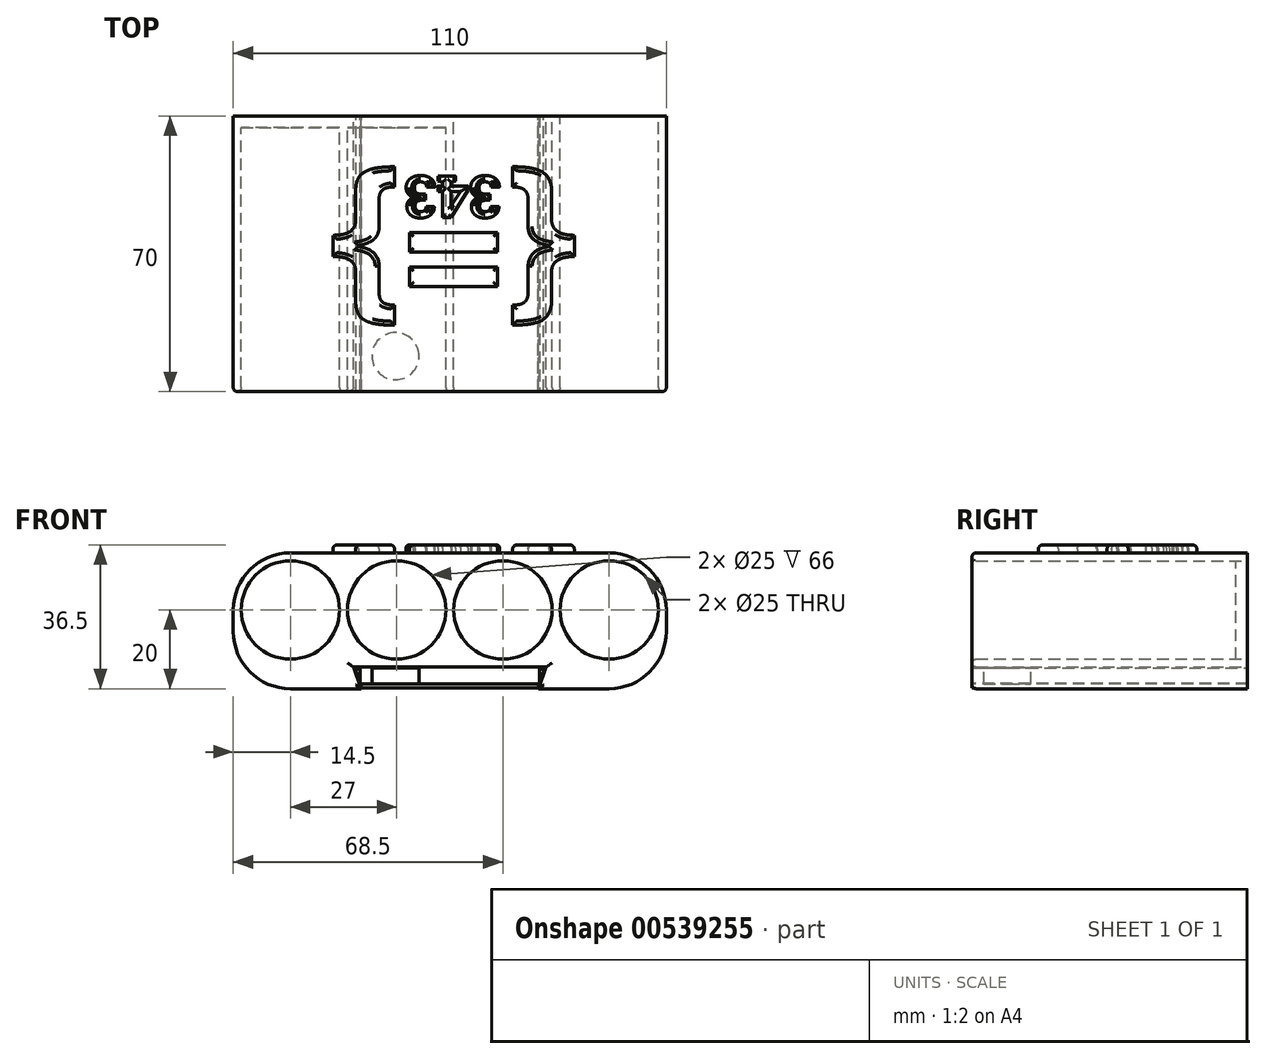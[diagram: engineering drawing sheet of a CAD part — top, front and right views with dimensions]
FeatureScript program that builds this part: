
annotation { "Feature Type Name" : "Feature", "Feature Type Description" : "" }
export const myFeature = defineFeature(function(context is Context, id is Id, definition is map)
    precondition{}
    {
        {
            var Q0;
            Q0=qCreatedBy(makeId("Front.planeOp"),FACE);
            var sketch = newSketch(context, id + "F0", { "sketchPlane" : qUnion([Q0])});
            skLineSegment(sketch, "E0", {"start": v(-24.5, 5.5) * mm, "end": v(-22.5, 0) * mm});
            skLineSegment(sketch, "E1", {"start": v(-22.5, 0) * mm, "end": v(-40.5, 0) * mm});
            skLineSegment(sketch, "E2", {"start": v(-55, 14.5) * mm, "end": v(-55, 20) * mm});
            skPoint(sketch, "E3.visualSharp", {"position": v(-55, 34.5) * mm});
            skArc(sketch, "E3.filletArc", {"start": v(-40.5, 34.5) * mm, "mid": v(-50.75, 30.25) * mm, "end": v(-55, 20) * mm});
            skPoint(sketch, "E4.visualSharp", {"position": v(-55, 0) * mm});
            skArc(sketch, "E4.filletArc", {"start": v(-55, 14.5) * mm, "mid": v(-50.75, 4.25) * mm, "end": v(-40.5, 0) * mm});
            skCircle(sketch, "E5", {"center": v(-40.5, 20) * mm, "radius": 12.5 * mm});
            skCircle(sketch, "E6.1.0.0", {"center": v(-13.5, 20) * mm, "radius": 12.5 * mm});
            skLineSegment(sketch, "E6.direction1", {"start": v(-40.5, 20) * mm, "end": v(-13.5, 20) * mm, "construction": true});
            skLineSegment(sketch, "E7", {"start": v(-40.5, 34.5) * mm, "end": v(-40.5, 0) * mm, "construction": true});
            skLineSegment(sketch, "E8", {"start": v(-40.5, 34.5) * mm, "end": v(0, 34.5) * mm});
            skLineSegment(sketch, "E9", {"start": v(-24.5, 5.5) * mm, "end": v(0, 5.5) * mm});
            skCircle(sketch, "E10.MirrorC", {"center": v(40.5, 20) * mm, "radius": 12.5 * mm});
            skPoint(sketch, "E11.MirrorP", {"position": v(55, 34.5) * mm});
            skLineSegment(sketch, "E12.MirrorCS", {"start": v(22.5, 0) * mm, "end": v(40.5, 0) * mm});
            skArc(sketch, "E13.MirrorCS", {"start": v(55, 14.5) * mm, "mid": v(50.75, 4.25) * mm, "end": v(40.5, 0) * mm});
            skPoint(sketch, "E14.MirrorP", {"position": v(55, 0) * mm});
            skLineSegment(sketch, "E15.MirrorCS", {"start": v(24.5, 5.5) * mm, "end": v(0, 5.5) * mm});
            skArc(sketch, "E16.MirrorCS", {"start": v(40.5, 34.5) * mm, "mid": v(50.75, 30.25) * mm, "end": v(55, 20) * mm});
            skLineSegment(sketch, "E17.MirrorCS", {"start": v(55, 14.5) * mm, "end": v(55, 20) * mm});
            skLineSegment(sketch, "E18.MirrorCS", {"start": v(40.5, 34.5) * mm, "end": v(40.5, 0) * mm, "construction": true});
            skLineSegment(sketch, "E19.MirrorCS", {"start": v(40.5, 34.5) * mm, "end": v(0, 34.5) * mm});
            skLineSegment(sketch, "E20.MirrorCS", {"start": v(24.5, 5.5) * mm, "end": v(22.5, 0) * mm});
            skCircle(sketch, "E21.MirrorC", {"center": v(13.5, 20) * mm, "radius": 12.5 * mm});
            skLineSegment(sketch, "E22.MirrorCS", {"start": v(40.5, 20) * mm, "end": v(13.5, 20) * mm, "construction": true});
            skSolve(sketch);
        }
        {
            var Q0;
            Q0=qSketchRegion(id+"F0",true);
            extrude(context, id + "F1", {"entities" : qUnion([Q0]), "depth" : 70 * mm, "offsetDistance" : 25 * mm, "hasSecondDirection" : true, "secondDirectionOppositeDirection" : false, "secondDirectionDepth" : 3 * mm});
        }
        {
            var Q0;
            Q0=makeQuery(id+"F0.imprint","IMPRINT",FACE,{"disambiguationData":[TD([[makeQuery(id+"F0.imprint","IMPRINT",EDGE,{"derivedFrom":sQuery(id+"F0.wireOp",EDGE,"E0")}),-1.0]])]});
            var Q1;
            Q1=makeQuery(id+"F0.imprint","IMPRINT",FACE,{"disambiguationData":[TD([[makeQuery(id+"F0.imprint","IMPRINT",EDGE,{"derivedFrom":sQuery(id+"F0.wireOp",EDGE,"E5")}),1.0]])]});
            var Q2;
            Q2=makeQuery(id+"F0.imprint","IMPRINT",FACE,{"disambiguationData":[TD([[makeQuery(id+"F0.imprint","IMPRINT",EDGE,{"derivedFrom":sQuery(id+"F0.wireOp",EDGE,"E6.1.0.0")}),1.0]])]});
            var Q3;
            Q3=makeQuery(id+"F0.imprint","IMPRINT",FACE,{"disambiguationData":[TD([[makeQuery(id+"F0.imprint","IMPRINT",EDGE,{"derivedFrom":sQuery(id+"F0.wireOp",EDGE,"E21.MirrorC")}),-1.0]])]});
            var Q4;
            Q4=makeQuery(id+"F0.imprint","IMPRINT",FACE,{"disambiguationData":[TD([[makeQuery(id+"F0.imprint","IMPRINT",EDGE,{"derivedFrom":sQuery(id+"F0.wireOp",EDGE,"E10.MirrorC")}),-1.0]])]});
            extrude(context, id + "F2", {"entities" : qUnion([Q0, Q1, Q2, Q3, Q4]), "operationType" : NewBodyOperationType.ADD, "depth" : 3 * mm, "offsetDistance" : 25 * mm});
        }
        {
            var Q0;
            Q0=makeQuery(id+"F1.opExtrude","SWEPT_FACE",FACE,{"disambiguationData":[OSD([sQuery(id+"F0.wireOp",EDGE,"E8"),sQuery(id+"F0.wireOp",EDGE,"E19.MirrorCS")])]});
            var sketch = newSketch(context, id + "F3", { "sketchPlane" : qUnion([Q0])});
            skText(sketch, "E23", { "text": "{=}", "fontName": "OpenSans-Bold.ttf"});
            skText(sketch, "E24", { "text": "343", "fontName": "RobotoSlab-Bold.ttf"});
            const initialGuessF3  = {"E23": [0.03232, -0.0202, -1, 0, 0.03322], "E24": [0.013, -0.01524, -1, 0, 0.01067]};
            skSetInitialGuess(sketch, initialGuessF3);
            skSolve(sketch);
        }
        {
            var Q0;
            Q0=qSketchRegion(id+"F3",true);
            extrude(context, id + "F4", {"entities" : qUnion([Q0]), "operationType" : NewBodyOperationType.ADD, "depth" : 2 * mm, "offsetDistance" : 25 * mm});
        }
        {
            var Q0;
            Q0=makeQuery(id+"F4.opExtrude","CAP_FACE",FACE,{"disambiguationData":[OSD([sQuery(id+"F3.wireOp",EDGE,"E23.sketch_text.stroke-0"),sQuery(id+"F3.wireOp",EDGE,"E23.sketch_text.stroke-1"),sQuery(id+"F3.wireOp",EDGE,"E23.sketch_text.stroke-2"),sQuery(id+"F3.wireOp",EDGE,"E23.sketch_text.stroke-3"),sQuery(id+"F3.wireOp",EDGE,"E23.sketch_text.stroke-4"),sQuery(id+"F3.wireOp",EDGE,"E23.sketch_text.stroke-5"),sQuery(id+"F3.wireOp",EDGE,"E23.sketch_text.stroke-6"),sQuery(id+"F3.wireOp",EDGE,"E23.sketch_text.stroke-7"),sQuery(id+"F3.wireOp",EDGE,"E23.sketch_text.stroke-8"),sQuery(id+"F3.wireOp",EDGE,"E23.sketch_text.stroke-9"),sQuery(id+"F3.wireOp",EDGE,"E23.sketch_text.stroke-10"),sQuery(id+"F3.wireOp",EDGE,"E23.sketch_text.stroke-11"),sQuery(id+"F3.wireOp",EDGE,"E23.sketch_text.stroke-12"),sQuery(id+"F3.wireOp",EDGE,"E23.sketch_text.stroke-13"),sQuery(id+"F3.wireOp",EDGE,"E23.sketch_text.stroke-14"),sQuery(id+"F3.wireOp",EDGE,"E23.sketch_text.stroke-15"),sQuery(id+"F3.wireOp",EDGE,"E23.sketch_text.stroke-16"),sQuery(id+"F3.wireOp",EDGE,"E23.sketch_text.stroke-17"),sQuery(id+"F3.wireOp",EDGE,"E23.sketch_text.stroke-18"),sQuery(id+"F3.wireOp",EDGE,"E23.sketch_text.stroke-19"),sQuery(id+"F3.wireOp",EDGE,"E23.sketch_text.stroke-20"),sQuery(id+"F3.wireOp",EDGE,"E23.sketch_text.stroke-21"),sQuery(id+"F3.wireOp",EDGE,"E23.sketch_text.stroke-22"),sQuery(id+"F3.wireOp",EDGE,"E23.sketch_text.stroke-23")])],"isStart":false});
            var Q1;
            Q1=makeQuery(id+"F4.opExtrude","CAP_FACE",FACE,{"disambiguationData":[OSD([sQuery(id+"F3.wireOp",EDGE,"E23.sketch_text.stroke-24"),sQuery(id+"F3.wireOp",EDGE,"E23.sketch_text.stroke-25"),sQuery(id+"F3.wireOp",EDGE,"E23.sketch_text.stroke-26"),sQuery(id+"F3.wireOp",EDGE,"E23.sketch_text.stroke-27")])],"isStart":false});
            var Q2;
            Q2=makeQuery(id+"F4.opExtrude","CAP_FACE",FACE,{"disambiguationData":[OSD([sQuery(id+"F3.wireOp",EDGE,"E23.sketch_text.stroke-28"),sQuery(id+"F3.wireOp",EDGE,"E23.sketch_text.stroke-29"),sQuery(id+"F3.wireOp",EDGE,"E23.sketch_text.stroke-30"),sQuery(id+"F3.wireOp",EDGE,"E23.sketch_text.stroke-31")])],"isStart":false});
            var Q3;
            Q3=makeQuery(id+"F4.opExtrude","CAP_FACE",FACE,{"disambiguationData":[OSD([sQuery(id+"F3.wireOp",EDGE,"E23.sketch_text.stroke-32"),sQuery(id+"F3.wireOp",EDGE,"E23.sketch_text.stroke-33"),sQuery(id+"F3.wireOp",EDGE,"E23.sketch_text.stroke-34"),sQuery(id+"F3.wireOp",EDGE,"E23.sketch_text.stroke-35"),sQuery(id+"F3.wireOp",EDGE,"E23.sketch_text.stroke-36"),sQuery(id+"F3.wireOp",EDGE,"E23.sketch_text.stroke-37"),sQuery(id+"F3.wireOp",EDGE,"E23.sketch_text.stroke-38"),sQuery(id+"F3.wireOp",EDGE,"E23.sketch_text.stroke-39"),sQuery(id+"F3.wireOp",EDGE,"E23.sketch_text.stroke-40"),sQuery(id+"F3.wireOp",EDGE,"E23.sketch_text.stroke-41"),sQuery(id+"F3.wireOp",EDGE,"E23.sketch_text.stroke-42"),sQuery(id+"F3.wireOp",EDGE,"E23.sketch_text.stroke-43"),sQuery(id+"F3.wireOp",EDGE,"E23.sketch_text.stroke-44"),sQuery(id+"F3.wireOp",EDGE,"E23.sketch_text.stroke-45"),sQuery(id+"F3.wireOp",EDGE,"E23.sketch_text.stroke-46"),sQuery(id+"F3.wireOp",EDGE,"E23.sketch_text.stroke-47"),sQuery(id+"F3.wireOp",EDGE,"E23.sketch_text.stroke-48"),sQuery(id+"F3.wireOp",EDGE,"E23.sketch_text.stroke-49"),sQuery(id+"F3.wireOp",EDGE,"E23.sketch_text.stroke-50"),sQuery(id+"F3.wireOp",EDGE,"E23.sketch_text.stroke-51"),sQuery(id+"F3.wireOp",EDGE,"E23.sketch_text.stroke-52"),sQuery(id+"F3.wireOp",EDGE,"E23.sketch_text.stroke-53"),sQuery(id+"F3.wireOp",EDGE,"E23.sketch_text.stroke-54"),sQuery(id+"F3.wireOp",EDGE,"E23.sketch_text.stroke-55"),sQuery(id+"F3.wireOp",EDGE,"E23.sketch_text.stroke-56"),sQuery(id+"F3.wireOp",EDGE,"E23.sketch_text.stroke-57"),sQuery(id+"F3.wireOp",EDGE,"E23.sketch_text.stroke-58")])],"isStart":false});
            var Q4;
            Q4=makeQuery(id+"F1.opExtrude","CAP_FACE",FACE,{"disambiguationData":[OSD([sQuery(id+"F0.wireOp",EDGE,"E0"),sQuery(id+"F0.wireOp",EDGE,"E1"),sQuery(id+"F0.wireOp",EDGE,"E2"),sQuery(id+"F0.wireOp",EDGE,"E3.filletArc"),sQuery(id+"F0.wireOp",EDGE,"E4.filletArc"),sQuery(id+"F0.wireOp",EDGE,"E5"),sQuery(id+"F0.wireOp",EDGE,"E6.1.0.0"),sQuery(id+"F0.wireOp",EDGE,"E8"),sQuery(id+"F0.wireOp",EDGE,"E9"),sQuery(id+"F0.wireOp",EDGE,"E10.MirrorC"),sQuery(id+"F0.wireOp",EDGE,"E12.MirrorCS"),sQuery(id+"F0.wireOp",EDGE,"E13.MirrorCS"),sQuery(id+"F0.wireOp",EDGE,"E15.MirrorCS"),sQuery(id+"F0.wireOp",EDGE,"E16.MirrorCS"),sQuery(id+"F0.wireOp",EDGE,"E17.MirrorCS"),sQuery(id+"F0.wireOp",EDGE,"E19.MirrorCS"),sQuery(id+"F0.wireOp",EDGE,"E20.MirrorCS"),sQuery(id+"F0.wireOp",EDGE,"E21.MirrorC")])],"isStart":false});
            fillet(context, id + "F5", {"entities" : qUnion([Q0, Q1, Q2, Q3, Q4]), "radius" : 1 * mm, "tangentPropagation" : true, "allowEdgeOverflow" : false});
        }
        {
            var Q0;
            Q0=makeQuery(id+"F4.opExtrude","CAP_FACE",FACE,{"disambiguationData":[OSD([sQuery(id+"F3.wireOp",EDGE,"E24.sketch_text.stroke-0"),sQuery(id+"F3.wireOp",EDGE,"E24.sketch_text.stroke-1"),sQuery(id+"F3.wireOp",EDGE,"E24.sketch_text.stroke-2"),sQuery(id+"F3.wireOp",EDGE,"E24.sketch_text.stroke-3"),sQuery(id+"F3.wireOp",EDGE,"E24.sketch_text.stroke-4"),sQuery(id+"F3.wireOp",EDGE,"E24.sketch_text.stroke-5"),sQuery(id+"F3.wireOp",EDGE,"E24.sketch_text.stroke-6"),sQuery(id+"F3.wireOp",EDGE,"E24.sketch_text.stroke-7"),sQuery(id+"F3.wireOp",EDGE,"E24.sketch_text.stroke-8"),sQuery(id+"F3.wireOp",EDGE,"E24.sketch_text.stroke-9"),sQuery(id+"F3.wireOp",EDGE,"E24.sketch_text.stroke-10"),sQuery(id+"F3.wireOp",EDGE,"E24.sketch_text.stroke-11"),sQuery(id+"F3.wireOp",EDGE,"E24.sketch_text.stroke-12"),sQuery(id+"F3.wireOp",EDGE,"E24.sketch_text.stroke-13"),sQuery(id+"F3.wireOp",EDGE,"E24.sketch_text.stroke-14"),sQuery(id+"F3.wireOp",EDGE,"E24.sketch_text.stroke-15"),sQuery(id+"F3.wireOp",EDGE,"E24.sketch_text.stroke-16"),sQuery(id+"F3.wireOp",EDGE,"E24.sketch_text.stroke-17"),sQuery(id+"F3.wireOp",EDGE,"E24.sketch_text.stroke-18"),sQuery(id+"F3.wireOp",EDGE,"E24.sketch_text.stroke-19"),sQuery(id+"F3.wireOp",EDGE,"E24.sketch_text.stroke-20"),sQuery(id+"F3.wireOp",EDGE,"E24.sketch_text.stroke-21"),sQuery(id+"F3.wireOp",EDGE,"E24.sketch_text.stroke-22"),sQuery(id+"F3.wireOp",EDGE,"E24.sketch_text.stroke-23"),sQuery(id+"F3.wireOp",EDGE,"E24.sketch_text.stroke-24"),sQuery(id+"F3.wireOp",EDGE,"E24.sketch_text.stroke-25"),sQuery(id+"F3.wireOp",EDGE,"E24.sketch_text.stroke-26"),sQuery(id+"F3.wireOp",EDGE,"E24.sketch_text.stroke-27"),sQuery(id+"F3.wireOp",EDGE,"E24.sketch_text.stroke-28"),sQuery(id+"F3.wireOp",EDGE,"E24.sketch_text.stroke-29"),sQuery(id+"F3.wireOp",EDGE,"E24.sketch_text.stroke-30")])],"isStart":false});
            var Q1;
            Q1=makeQuery(id+"F4.opExtrude","CAP_FACE",FACE,{"disambiguationData":[OSD([sQuery(id+"F3.wireOp",EDGE,"E24.sketch_text.stroke-51"),sQuery(id+"F3.wireOp",EDGE,"E24.sketch_text.stroke-52"),sQuery(id+"F3.wireOp",EDGE,"E24.sketch_text.stroke-53"),sQuery(id+"F3.wireOp",EDGE,"E24.sketch_text.stroke-54"),sQuery(id+"F3.wireOp",EDGE,"E24.sketch_text.stroke-55"),sQuery(id+"F3.wireOp",EDGE,"E24.sketch_text.stroke-56"),sQuery(id+"F3.wireOp",EDGE,"E24.sketch_text.stroke-57"),sQuery(id+"F3.wireOp",EDGE,"E24.sketch_text.stroke-58"),sQuery(id+"F3.wireOp",EDGE,"E24.sketch_text.stroke-59"),sQuery(id+"F3.wireOp",EDGE,"E24.sketch_text.stroke-60"),sQuery(id+"F3.wireOp",EDGE,"E24.sketch_text.stroke-61"),sQuery(id+"F3.wireOp",EDGE,"E24.sketch_text.stroke-62"),sQuery(id+"F3.wireOp",EDGE,"E24.sketch_text.stroke-63"),sQuery(id+"F3.wireOp",EDGE,"E24.sketch_text.stroke-64"),sQuery(id+"F3.wireOp",EDGE,"E24.sketch_text.stroke-65"),sQuery(id+"F3.wireOp",EDGE,"E24.sketch_text.stroke-66"),sQuery(id+"F3.wireOp",EDGE,"E24.sketch_text.stroke-67"),sQuery(id+"F3.wireOp",EDGE,"E24.sketch_text.stroke-68"),sQuery(id+"F3.wireOp",EDGE,"E24.sketch_text.stroke-69"),sQuery(id+"F3.wireOp",EDGE,"E24.sketch_text.stroke-70"),sQuery(id+"F3.wireOp",EDGE,"E24.sketch_text.stroke-71"),sQuery(id+"F3.wireOp",EDGE,"E24.sketch_text.stroke-72"),sQuery(id+"F3.wireOp",EDGE,"E24.sketch_text.stroke-73"),sQuery(id+"F3.wireOp",EDGE,"E24.sketch_text.stroke-74"),sQuery(id+"F3.wireOp",EDGE,"E24.sketch_text.stroke-75"),sQuery(id+"F3.wireOp",EDGE,"E24.sketch_text.stroke-76"),sQuery(id+"F3.wireOp",EDGE,"E24.sketch_text.stroke-77"),sQuery(id+"F3.wireOp",EDGE,"E24.sketch_text.stroke-78"),sQuery(id+"F3.wireOp",EDGE,"E24.sketch_text.stroke-79"),sQuery(id+"F3.wireOp",EDGE,"E24.sketch_text.stroke-80"),sQuery(id+"F3.wireOp",EDGE,"E24.sketch_text.stroke-81")])],"isStart":false});
            var Q2;
            Q2=makeQuery(id+"F4.opExtrude","CAP_FACE",FACE,{"disambiguationData":[OSD([sQuery(id+"F3.wireOp",EDGE,"E24.sketch_text.stroke-31"),sQuery(id+"F3.wireOp",EDGE,"E24.sketch_text.stroke-32"),sQuery(id+"F3.wireOp",EDGE,"E24.sketch_text.stroke-33"),sQuery(id+"F3.wireOp",EDGE,"E24.sketch_text.stroke-34"),sQuery(id+"F3.wireOp",EDGE,"E24.sketch_text.stroke-35"),sQuery(id+"F3.wireOp",EDGE,"E24.sketch_text.stroke-36"),sQuery(id+"F3.wireOp",EDGE,"E24.sketch_text.stroke-37"),sQuery(id+"F3.wireOp",EDGE,"E24.sketch_text.stroke-38"),sQuery(id+"F3.wireOp",EDGE,"E24.sketch_text.stroke-39"),sQuery(id+"F3.wireOp",EDGE,"E24.sketch_text.stroke-40"),sQuery(id+"F3.wireOp",EDGE,"E24.sketch_text.stroke-41"),sQuery(id+"F3.wireOp",EDGE,"E24.sketch_text.stroke-42"),sQuery(id+"F3.wireOp",EDGE,"E24.sketch_text.stroke-43"),sQuery(id+"F3.wireOp",EDGE,"E24.sketch_text.stroke-44"),sQuery(id+"F3.wireOp",EDGE,"E24.sketch_text.stroke-45"),sQuery(id+"F3.wireOp",EDGE,"E24.sketch_text.stroke-46"),sQuery(id+"F3.wireOp",EDGE,"E24.sketch_text.stroke-47"),sQuery(id+"F3.wireOp",EDGE,"E24.sketch_text.stroke-48"),sQuery(id+"F3.wireOp",EDGE,"E24.sketch_text.stroke-49"),sQuery(id+"F3.wireOp",EDGE,"E24.sketch_text.stroke-50")])],"isStart":false});
            fillet(context, id + "F6", {"entities" : qUnion([Q0, Q1, Q2]), "radius" : 0.7 * mm, "tangentPropagation" : true, "allowEdgeOverflow" : false});
        }
        {
            var Q0;
            Q0=qCreatedBy(makeId("Front.planeOp"),FACE);
            var sketch = newSketch(context, id + "F7", { "sketchPlane" : qUnion([Q0])});
            skLineSegment(sketch, "E25.0", {"start": v(-24.5, 5.5) * mm, "end": v(0, 5.5) * mm});
            skLineSegment(sketch, "E26.0", {"start": v(-24.5, 5.5) * mm, "end": v(-22.5, 0) * mm});
            skLineSegment(sketch, "E27", {"start": v(-22.5, 0) * mm, "end": v(0, 0) * mm, "construction": true});
            skLineSegment(sketch, "E28.0", {"start": v(-22.79, 5.3) * mm, "end": v(0, 5.3) * mm});
            skLineSegment(sketch, "E28.1", {"start": v(-23.73, 3.96) * mm, "end": v(-22.36, 0.2) * mm});
            skLineSegment(sketch, "E28.2", {"start": v(-22.36, 0.2) * mm, "end": v(0, 0.2) * mm});
            skPoint(sketch, "E29.visualSharp", {"position": v(-24.21, 5.3) * mm});
            skArc(sketch, "E29.filletArc", {"start": v(-22.79, 5.3) * mm, "mid": v(-23.6, 4.87) * mm, "end": v(-23.73, 3.96) * mm});
            skLineSegment(sketch, "E30.MirrorCS", {"start": v(22.79, 5.3) * mm, "end": v(0, 5.3) * mm});
            skArc(sketch, "E31.MirrorCS", {"start": v(22.79, 5.3) * mm, "mid": v(23.6, 4.87) * mm, "end": v(23.73, 3.96) * mm});
            skLineSegment(sketch, "E32.MirrorCS", {"start": v(23.73, 3.96) * mm, "end": v(22.36, 0.2) * mm});
            skLineSegment(sketch, "E33.MirrorCS", {"start": v(22.36, 0.2) * mm, "end": v(0, 0.2) * mm});
            skSolve(sketch);
        }
        {
            var Q0;
            Q0=makeQuery(id+"F7.imprint","IMPRINT",FACE,{"disambiguationData":[TD([[makeQuery(id+"F7.imprint","IMPRINT",EDGE,{"derivedFrom":sQuery(id+"F7.wireOp",EDGE,"E28.0")}),-1.0]])]});
            var Q1;
            Q1=makeQuery(id+"F5.opFillet","SPLIT",FACE,{"disambiguationData":[OD(1.0)],"derivedFrom":makeQuery(id+"F1.opExtrude","CAP_FACE",FACE,{"disambiguationData":[OSD([sQuery(id+"F0.wireOp",EDGE,"E0"),sQuery(id+"F0.wireOp",EDGE,"E1"),sQuery(id+"F0.wireOp",EDGE,"E2"),sQuery(id+"F0.wireOp",EDGE,"E3.filletArc"),sQuery(id+"F0.wireOp",EDGE,"E4.filletArc"),sQuery(id+"F0.wireOp",EDGE,"E5"),sQuery(id+"F0.wireOp",EDGE,"E6.1.0.0"),sQuery(id+"F0.wireOp",EDGE,"E8"),sQuery(id+"F0.wireOp",EDGE,"E9"),sQuery(id+"F0.wireOp",EDGE,"E10.MirrorC"),sQuery(id+"F0.wireOp",EDGE,"E12.MirrorCS"),sQuery(id+"F0.wireOp",EDGE,"E13.MirrorCS"),sQuery(id+"F0.wireOp",EDGE,"E15.MirrorCS"),sQuery(id+"F0.wireOp",EDGE,"E16.MirrorCS"),sQuery(id+"F0.wireOp",EDGE,"E17.MirrorCS"),sQuery(id+"F0.wireOp",EDGE,"E19.MirrorCS"),sQuery(id+"F0.wireOp",EDGE,"E20.MirrorCS"),sQuery(id+"F0.wireOp",EDGE,"E21.MirrorC")])],"isStart":false})});
            extrude(context, id + "F8", {"entities" : qUnion([Q0]), "endBound" : BoundingType.UP_TO_SURFACE, "depth" : 25 * mm, "endBoundEntityFace" : qUnion([Q1]), "offsetDistance" : 25 * mm});
        }
        {
            var Q0;
            Q0=makeQuery(id+"F8.opExtrude","SWEPT_FACE",FACE,{"disambiguationData":[OSD([sQuery(id+"F7.wireOp",EDGE,"E28.0"),sQuery(id+"F7.wireOp",EDGE,"E30.MirrorCS")])]});
            var sketch = newSketch(context, id + "F9", { "sketchPlane" : qUnion([Q0])});
            skCircle(sketch, "E34", {"center": v(13.79, -61) * mm, "radius": 6 * mm});
            skCircle(sketch, "E35.MirrorC", {"center": v(-13.79, -61) * mm, "radius": 6 * mm});
            skSolve(sketch);
        }
        {
            var Q0;
            Q0=makeQuery(id+"F9.imprint","IMPRINT",FACE,{"disambiguationData":[TD([[makeQuery(id+"F9.imprint","IMPRINT",EDGE,{"derivedFrom":sQuery(id+"F9.wireOp",EDGE,"E35.MirrorC")}),-1.0]])]});
            var Q1;
            Q1=makeQuery(id+"F9.imprint","IMPRINT",FACE,{"disambiguationData":[TD([[makeQuery(id+"F9.imprint","IMPRINT",EDGE,{"derivedFrom":sQuery(id+"F9.wireOp",EDGE,"E34")}),1.0]])]});
            var Q2;
            Q2=makeQuery(id+"F8.opExtrude","SWEPT_FACE",FACE,{"disambiguationData":[OSD([sQuery(id+"F7.wireOp",EDGE,"E28.2"),sQuery(id+"F7.wireOp",EDGE,"E33.MirrorCS")])]});
            extrude(context, id + "F10", {"entities" : qUnion([Q0, Q1]), "operationType" : NewBodyOperationType.REMOVE, "endBound" : BoundingType.UP_TO_SURFACE, "oppositeDirection" : true, "depth" : 4 * mm, "endBoundEntityFace" : qUnion([Q2]), "hasOffset" : true, "offsetDistance" : 1 * mm});
        }
    });
